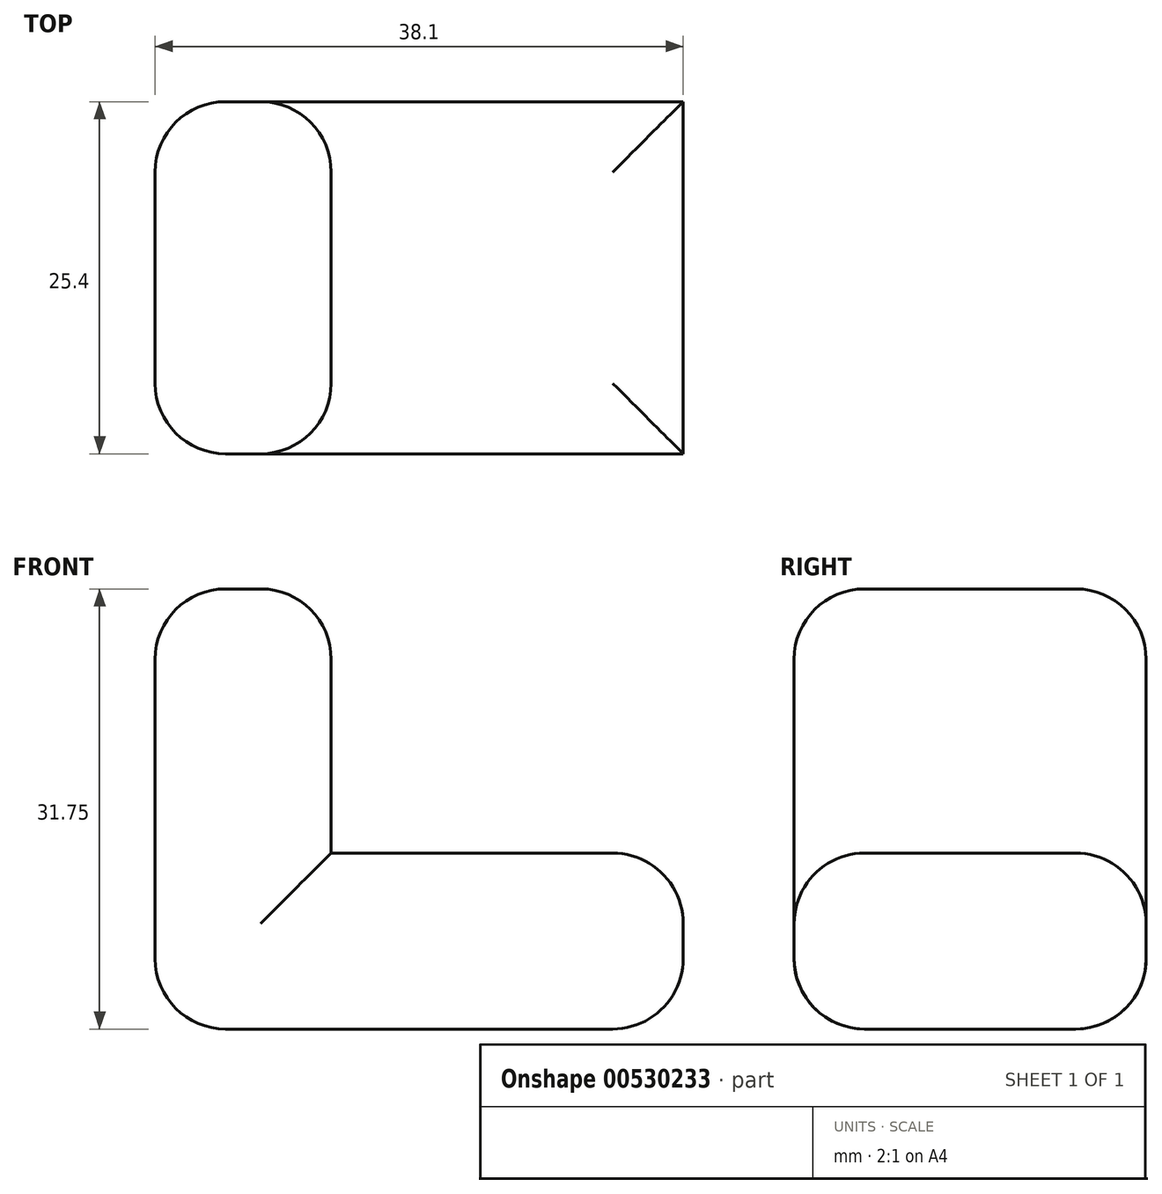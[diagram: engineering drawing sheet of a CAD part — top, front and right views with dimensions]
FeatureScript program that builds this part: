
annotation { "Feature Type Name" : "Feature", "Feature Type Description" : "" }
export const myFeature = defineFeature(function(context is Context, id is Id, definition is map)
    precondition{}
    {
        {
            var Q0;
            Q0=qCreatedBy(makeId("Front.planeOp"),FACE);
            var sketch = newSketch(context, id + "F0", { "sketchPlane" : qUnion([Q0])});
            skLineSegment(sketch, "E0", {"start": v(-41.1, 0) * mm, "end": v(-6.35, 0) * mm});
            skLineSegment(sketch, "E1", {"start": v(-6.35, 0) * mm, "end": v(-6.35, 12.7) * mm});
            skLineSegment(sketch, "E2", {"start": v(-6.35, 12.7) * mm, "end": v(-31.75, 12.7) * mm});
            skLineSegment(sketch, "E3", {"start": v(-31.75, 12.7) * mm, "end": v(-31.75, 31.75) * mm});
            skLineSegment(sketch, "E4", {"start": v(-31.75, 31.75) * mm, "end": v(-44.45, 31.75) * mm});
            skLineSegment(sketch, "E5", {"start": v(-44.45, 31.75) * mm, "end": v(-44.45, 0) * mm});
            skLineSegment(sketch, "E6", {"start": v(-44.45, 0) * mm, "end": v(-41.1, 0) * mm});
            skSolve(sketch);
        }
        {
            var Q0;
            Q0 = qSketchRegion(id + "F0", true);
            extrude(context, id + "F1", {"entities" : qUnion([Q0]), "depth" : 25.4 * mm, "offsetDistance" : 25.4 * mm});
        }
        {
            var Q0;
            Q0=makeQuery(id+"F1.opExtrude","CAP_EDGE",EDGE,{"disambiguationData":[OSD([sQuery(id+"F0.wireOp",EDGE,"E5")])],"isStart":false});
            var Q1;
            Q1=makeQuery(id+"F1.opExtrude","CAP_EDGE",EDGE,{"disambiguationData":[OSD([sQuery(id+"F0.wireOp",EDGE,"E3")])],"isStart":false});
            var Q2;
            Q2=makeQuery(id+"F1.opExtrude","CAP_EDGE",EDGE,{"disambiguationData":[OSD([sQuery(id+"F0.wireOp",EDGE,"E2")])],"isStart":false});
            var Q3;
            Q3=makeQuery(id+"F1.opExtrude","CAP_EDGE",EDGE,{"disambiguationData":[OSD([sQuery(id+"F0.wireOp",EDGE,"E5")])],"isStart":true});
            var Q4;
            Q4=makeQuery(id+"F1.opExtrude","CAP_EDGE",EDGE,{"disambiguationData":[OSD([sQuery(id+"F0.wireOp",EDGE,"E3")])],"isStart":true});
            var Q5;
            Q5=makeQuery(id+"F1.opExtrude","CAP_EDGE",EDGE,{"disambiguationData":[OSD([sQuery(id+"F0.wireOp",EDGE,"E2")])],"isStart":true});
            var Q6;
            Q6=makeQuery(id+"F1.opExtrude","SWEPT_EDGE",EDGE,{"disambiguationData":[OSD([sQuery(id+"F0.wireOp",EDGE,"E1"),sQuery(id+"F0.wireOp",EDGE,"E2")])]});
            var Q7;
            Q7=makeQuery(id+"F1.opExtrude","CAP_EDGE",EDGE,{"disambiguationData":[OSD([sQuery(id+"F0.wireOp",EDGE,"E0"),sQuery(id+"F0.wireOp",EDGE,"E6")])],"isStart":false});
            var Q8;
            Q8=makeQuery(id+"F1.opExtrude","SWEPT_EDGE",EDGE,{"disambiguationData":[OSD([sQuery(id+"F0.wireOp",EDGE,"E5"),sQuery(id+"F0.wireOp",EDGE,"E6")])]});
            var Q9;
            Q9=makeQuery(id+"F1.opExtrude","CAP_EDGE",EDGE,{"disambiguationData":[OSD([sQuery(id+"F0.wireOp",EDGE,"E0"),sQuery(id+"F0.wireOp",EDGE,"E6")])],"isStart":true});
            var Q10;
            Q10=makeQuery(id+"F1.opExtrude","SWEPT_EDGE",EDGE,{"disambiguationData":[OSD([sQuery(id+"F0.wireOp",EDGE,"E0"),sQuery(id+"F0.wireOp",EDGE,"E1")])]});
            var Q11;
            Q11=makeQuery(id+"F1.opExtrude","SWEPT_EDGE",EDGE,{"disambiguationData":[OSD([sQuery(id+"F0.wireOp",EDGE,"E3"),sQuery(id+"F0.wireOp",EDGE,"E4")])]});
            var Q12;
            Q12=makeQuery(id+"F1.opExtrude","SWEPT_FACE",FACE,{"disambiguationData":[OSD([sQuery(id+"F0.wireOp",EDGE,"E4")])]});
            fillet(context, id + "F2", {"entities" : qUnion([Q0, Q1, Q2, Q3, Q4, Q5, Q6, Q7, Q8, Q9, Q10, Q11, Q12]), "radius" : 5.08 * mm, "tangentPropagation" : true, "allowEdgeOverflow" : false});
        }
    });
